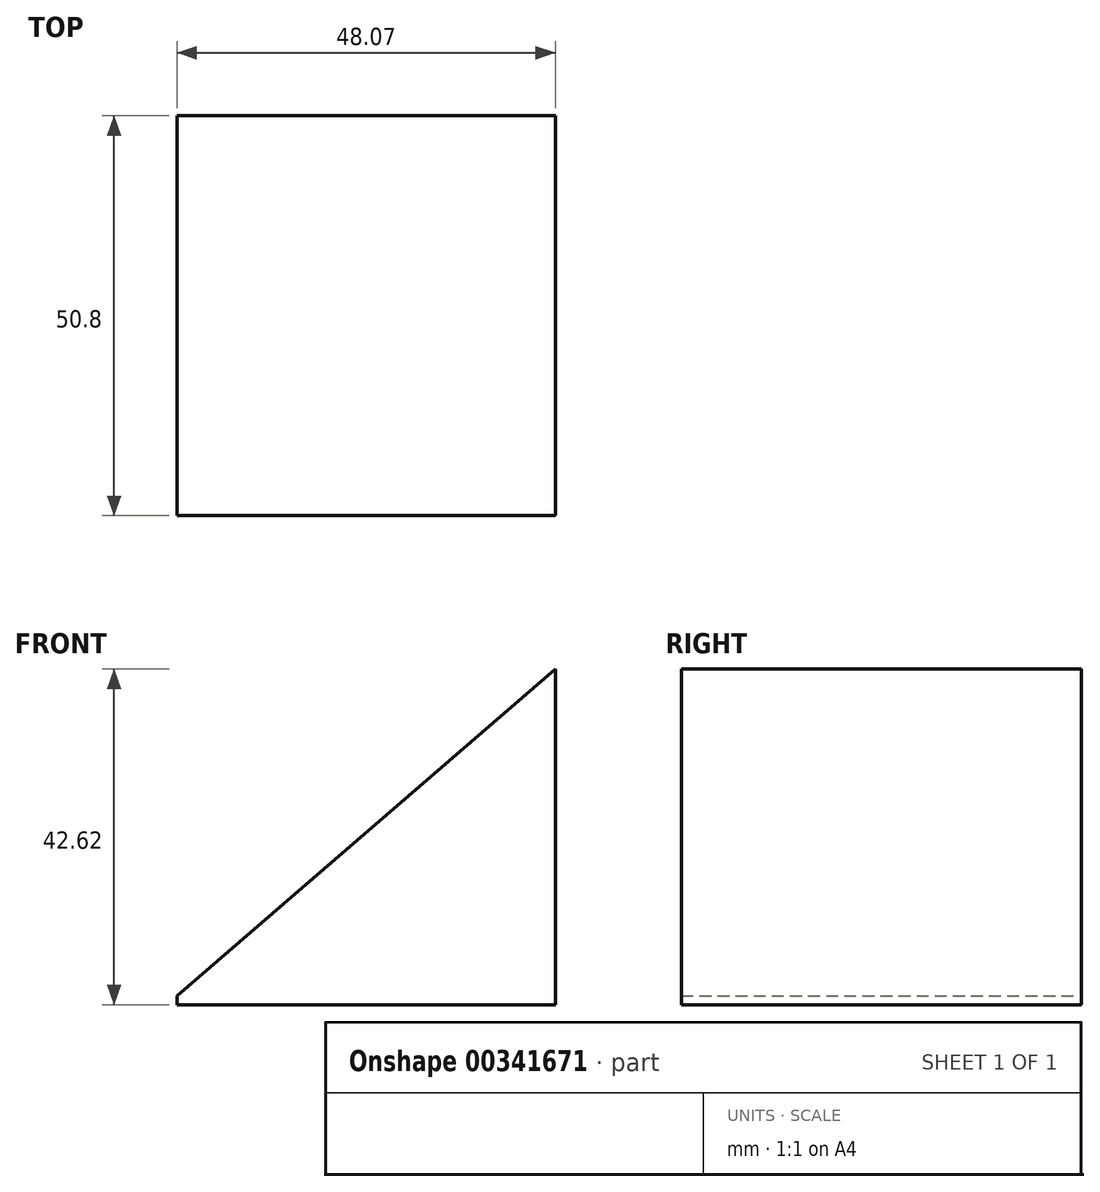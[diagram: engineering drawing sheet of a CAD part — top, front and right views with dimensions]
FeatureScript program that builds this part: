
annotation { "Feature Type Name" : "Feature", "Feature Type Description" : "" }
export const myFeature = defineFeature(function(context is Context, id is Id, definition is map)
    precondition{}
    {
        {
            var Q0;
            Q0=qCreatedBy(makeId("Front.planeOp"),FACE);
            var sketch = newSketch(context, id + "F0", { "sketchPlane" : qUnion([Q0])});
            skLineSegment(sketch, "E0", {"start": v(-42.02, 15.08) * mm, "end": v(6.05, 56.58) * mm});
            skLineSegment(sketch, "E1", {"start": v(6.05, 56.58) * mm, "end": v(6.05, 13.96) * mm});
            skLineSegment(sketch, "E2", {"start": v(6.05, 13.96) * mm, "end": v(-42.02, 13.96) * mm});
            skLineSegment(sketch, "E3", {"start": v(-42.02, 15.08) * mm, "end": v(-42.02, 13.96) * mm});
            skSolve(sketch);
        }
        {
            var Q0;
            Q0=makeQuery(id+"F0.imprint","IMPRINT",FACE,{"disambiguationData":[TD([[makeQuery(id+"F0.imprint","IMPRINT",EDGE,{"derivedFrom":sQuery(id+"F0.wireOp",EDGE,"E0")}),-1.0]])]});
            extrude(context, id + "F1", {"entities" : qUnion([Q0]), "depth" : 50.8 * mm, "offsetDistance" : 25.4 * mm});
        }
    });
